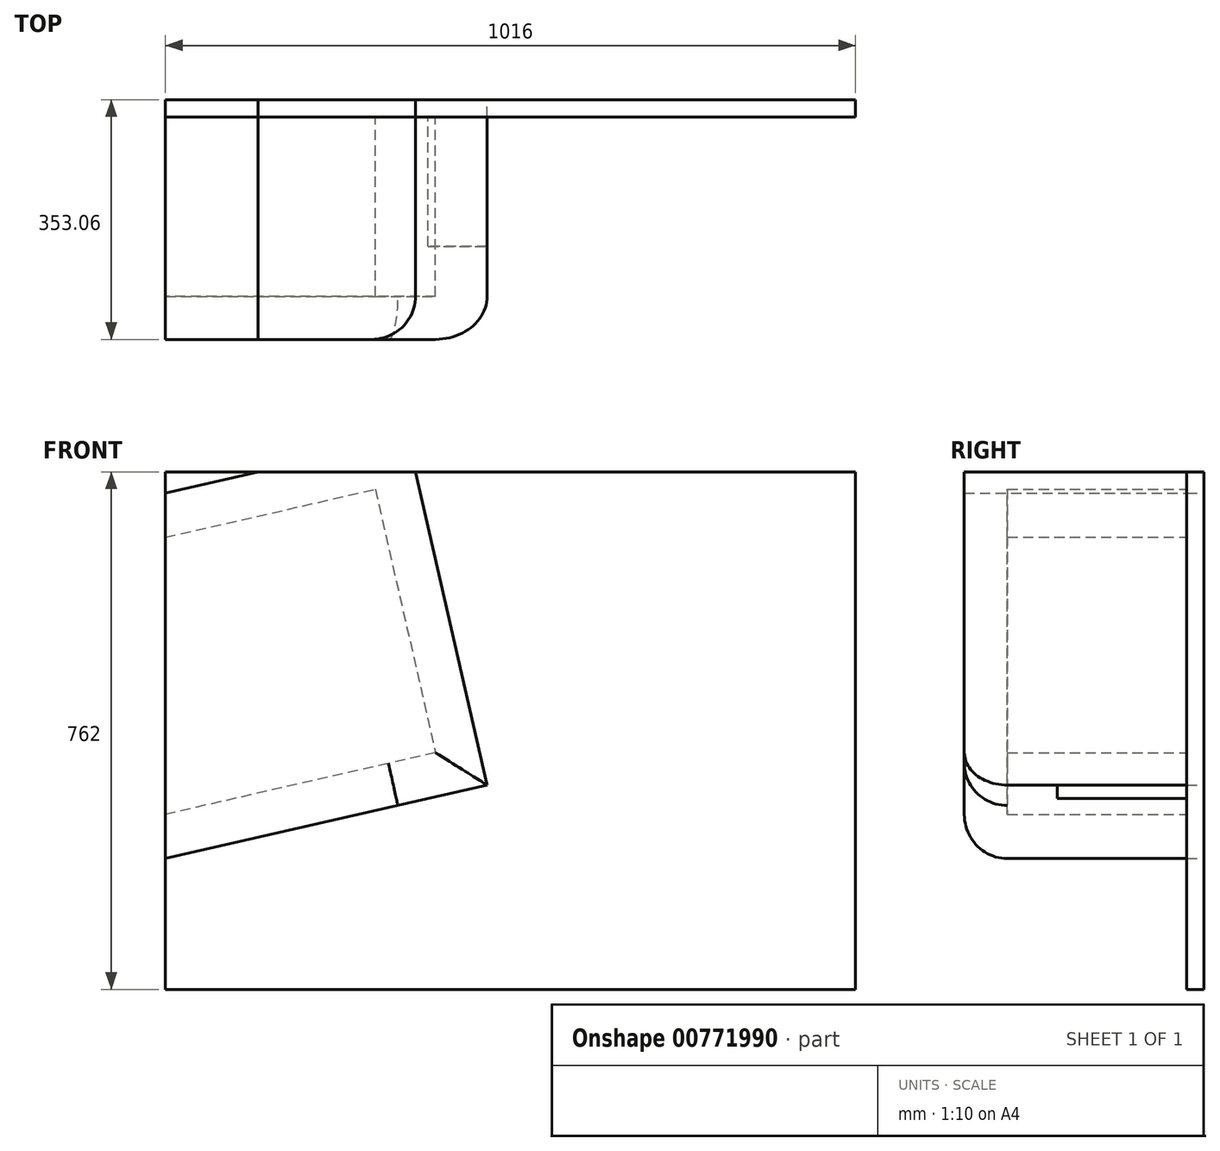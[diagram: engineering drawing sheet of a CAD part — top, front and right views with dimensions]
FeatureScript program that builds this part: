
annotation { "Feature Type Name" : "Feature", "Feature Type Description" : "" }
export const myFeature = defineFeature(function(context is Context, id is Id, definition is map)
    precondition{}
    {
        {
            var Q0;
            Q0=qCreatedBy(makeId("Front.planeOp"),FACE);
            var sketch = newSketch(context, id + "F0", { "sketchPlane" : qUnion([Q0])});
            skLineSegment(sketch, "E0.bottom", {"start": v(-68.95, 0) * mm, "end": v(-1084.95, 0) * mm});
            skLineSegment(sketch, "E0.top", {"start": v(-68.95, 762) * mm, "end": v(-1084.95, 762) * mm});
            skLineSegment(sketch, "E0.left", {"start": v(-68.95, 0) * mm, "end": v(-68.95, 762) * mm});
            skLineSegment(sketch, "E0.right", {"start": v(-1084.95, 0) * mm, "end": v(-1084.95, 762) * mm});
            skSolve(sketch);
        }
        {
            var Q0;
            Q0=makeQuery(id+"F0.imprint","IMPRINT",FACE,{"disambiguationData":[TD([[makeQuery(id+"F0.imprint","IMPRINT",EDGE,{"derivedFrom":sQuery(id+"F0.wireOp",EDGE,"E0.bottom")}),-1.0]])]});
            extrude(context, id + "F1", {"entities" : qUnion([Q0]), "depth" : 25.4 * mm, "offsetDistance" : 25.4 * mm});
        }
        {
            var Q0;
            Q0=makeQuery(id+"F1.opExtrude","CAP_FACE",FACE,{"disambiguationData":[OSD([sQuery(id+"F0.wireOp",EDGE,"E0.bottom"),sQuery(id+"F0.wireOp",EDGE,"E0.top"),sQuery(id+"F0.wireOp",EDGE,"E0.left"),sQuery(id+"F0.wireOp",EDGE,"E0.right")])],"isStart":false});
            var sketch = newSketch(context, id + "F2", { "sketchPlane" : qUnion([Q0])});
            skLineSegment(sketch, "E1", {"start": v(-1084.95, 665.71) * mm, "end": v(-845.45, 720.43) * mm});
            skLineSegment(sketch, "E2", {"start": v(-845.45, 720.43) * mm, "end": v(-756.87, 332.69) * mm});
            skLineSegment(sketch, "E3", {"start": v(-756.87, 332.69) * mm, "end": v(-1084.95, 257.73) * mm});
            skLineSegment(sketch, "E4", {"start": v(-1084.95, 665.71) * mm, "end": v(-776.09, 736.28) * mm});
            skLineSegment(sketch, "E5", {"start": v(-776.09, 736.28) * mm, "end": v(-687.5, 348.53) * mm});
            skLineSegment(sketch, "E6", {"start": v(-687.5, 348.53) * mm, "end": v(-756.87, 332.69) * mm});
            skSolve(sketch);
        }
        {
            var Q0;
            {var subQ0=sQuery(id+"F2.wireOp",EDGE,"E2");Q0=makeQuery(id+"F2.imprint","IMPRINT",FACE,{"disambiguationData":[TD([[makeQuery(id+"F2.imprint","IMPRINT",EDGE,{"derivedFrom":subQ0}),1.0]])]});}
            var Q1;
            {var subQ0=sQuery(id+"F2.wireOp",EDGE,"E2");Q1=makeQuery(id+"F2.imprint","IMPRINT",FACE,{"disambiguationData":[TD([[makeQuery(id+"F2.imprint","IMPRINT",EDGE,{"derivedFrom":subQ0}),-1.0]])]});}
            extrude(context, id + "F3", {"entities" : qUnion([Q0, Q1]), "depth" : 264.16 * mm, "offsetDistance" : 25.4 * mm});
        }
        {
            var Q0;
            Q0=makeQuery(id+"F3.opExtrude","SWEPT_FACE",FACE,{"disambiguationData":[OSD([sQuery(id+"F0.wireOp",EDGE,"E0.right")])]});
            shell(context, id + "F4", {"entities" : qUnion([Q0]), "thickness" : 63.5 * mm, "oppositeDirection" : true});
        }
        {
            var Q0;
            Q0=makeQuery(id+"F3.opExtrude","CAP_FACE",FACE,{"disambiguationData":[OSD([sQuery(id+"F0.wireOp",EDGE,"E0.right"),sQuery(id+"F2.wireOp",EDGE,"E3"),sQuery(id+"F2.wireOp",EDGE,"E4"),sQuery(id+"F2.wireOp",EDGE,"E5"),sQuery(id+"F2.wireOp",EDGE,"E6")])],"isStart":true});
            var Q1;
            {var subQ0=sQuery(id+"F2.wireOp",EDGE,"E6");var subQ1=sQuery(id+"F2.wireOp",EDGE,"E5");var subQ2=sQuery(id+"F2.wireOp",EDGE,"E4");var subQ3=sQuery(id+"F2.wireOp",EDGE,"E3");var subQ4=sQuery(id+"F0.wireOp",EDGE,"E0.right");Q1=makeQuery(id+"F4.opShell","OFFSET_FACE",FACE,{"disambiguationData":[OSD([subQ4,subQ3,subQ2,subQ1,subQ0]),TDD([makeQuery(id+"F3.opExtrude","CAP_FACE",FACE,{"disambiguationData":[OSD([subQ4,subQ3,subQ2,subQ1,subQ0])],"isStart":true})])]});}
            extrude(context, id + "F5", {"entities" : qUnion([Q0]), "operationType" : NewBodyOperationType.REMOVE, "endBound" : BoundingType.UP_TO_SURFACE, "oppositeDirection" : true, "depth" : 25.4 * mm, "endBoundEntityFace" : qUnion([Q1]), "offsetDistance" : 25.4 * mm});
        }
        {
            var Q0;
            Q0=makeQuery(id+"F5.boolean.opBoolean","COPY",FACE,{"derivedFrom":makeQuery(id+"F5.opExtrude","CAP_FACE",FACE,{"disambiguationData":[OSD([sQuery(id+"F0.wireOp",EDGE,"E0.right"),sQuery(id+"F2.wireOp",EDGE,"E3"),sQuery(id+"F2.wireOp",EDGE,"E4"),sQuery(id+"F2.wireOp",EDGE,"E5"),sQuery(id+"F2.wireOp",EDGE,"E6")])],"isStart":false})});
            var sketch = newSketch(context, id + "F6", { "sketchPlane" : qUnion([Q0])});
            skLineSegment(sketch, "E7", {"start": v(728.33, 812.32) * mm, "end": v(716.83, 762) * mm});
            skLineSegment(sketch, "E8", {"start": v(716.83, 762) * mm, "end": v(948.6, 762) * mm});
            skLineSegment(sketch, "E9", {"start": v(948.6, 762) * mm, "end": v(728.33, 812.32) * mm});
            skSolve(sketch);
        }
        {
            var Q0;
            Q0=makeQuery(id+"F6.imprint","IMPRINT",FACE,{"disambiguationData":[TD([[makeQuery(id+"F6.imprint","IMPRINT",EDGE,{"derivedFrom":sQuery(id+"F6.wireOp",EDGE,"E7")}),1.0]])]});
            extrude(context, id + "F7", {"entities" : qUnion([Q0]), "operationType" : NewBodyOperationType.REMOVE, "endBound" : BoundingType.THROUGH_ALL, "oppositeDirection" : true, "depth" : 25.4 * mm, "offsetDistance" : 25.4 * mm});
        }
        {
            var Q0;
            Q0=makeQuery(id+"F3.opExtrude","CAP_EDGE",EDGE,{"disambiguationData":[OSD([sQuery(id+"F2.wireOp",EDGE,"E3"),sQuery(id+"F2.wireOp",EDGE,"E6")])],"isStart":false});
            var Q1;
            Q1=makeQuery(id+"F3.opExtrude","CAP_EDGE",EDGE,{"disambiguationData":[OSD([sQuery(id+"F2.wireOp",EDGE,"E5")])],"isStart":false});
            fillet(context, id + "F8", {"entities" : qUnion([Q0, Q1]), "radius" : 63.5 * mm, "tangentPropagation" : true, "allowEdgeOverflow" : false});
        }
        {
            var Q0;
            Q0=makeQuery(id+"F1.opExtrude","CAP_FACE",FACE,{"disambiguationData":[OSD([sQuery(id+"F0.wireOp",EDGE,"E0.bottom"),sQuery(id+"F0.wireOp",EDGE,"E0.top"),sQuery(id+"F0.wireOp",EDGE,"E0.left"),sQuery(id+"F0.wireOp",EDGE,"E0.right")])],"isStart":false});
            var sketch = newSketch(context, id + "F9", { "sketchPlane" : qUnion([Q0])});
            skLineSegment(sketch, "E10", {"start": v(-698.43, 280.9) * mm, "end": v(-611.45, 300.77) * mm});
            skLineSegment(sketch, "E11", {"start": v(-611.45, 300.77) * mm, "end": v(-641.35, 431.65) * mm});
            skLineSegment(sketch, "E12", {"start": v(-641.35, 431.65) * mm, "end": v(-355.55, 235.03) * mm});
            skLineSegment(sketch, "E13", {"start": v(-355.55, 235.03) * mm, "end": v(-434.42, 130.1) * mm});
            skLineSegment(sketch, "E14", {"start": v(-434.42, 130.1) * mm, "end": v(-698.43, 280.9) * mm});
            skSolve(sketch);
        }
        {
            var Q0;
            Q0=makeQuery(id+"F9.imprint","IMPRINT",FACE,{"disambiguationData":[TD([[makeQuery(id+"F9.imprint","IMPRINT",EDGE,{"derivedFrom":sQuery(id+"F9.wireOp",EDGE,"E10")}),-1.0]])]});
            extrude(context, id + "F10", {"entities" : qUnion([Q0]), "depth" : 190.5 * mm, "offsetDistance" : 25.4 * mm});
        }
        {
            var Q0;
            Q0=makeQuery(id+"F10.opExtrude","SWEPT_FACE",FACE,{"disambiguationData":[OSD([sQuery(id+"F9.wireOp",EDGE,"E14")])]});
            var sketch = newSketch(context, id + "F11", { "sketchPlane" : qUnion([Q0])});
            skPoint(sketch, "E15.end.orphan", {"position": v(-441.75, 120.65) * mm});
            skLineSegment(sketch, "E16", {"start": v(-609.57, 215.9) * mm, "end": v(-407.55, 104.62) * mm});
            skLineSegment(sketch, "E17", {"start": v(-407.55, 104.62) * mm, "end": v(-407.55, 215.9) * mm});
            skLineSegment(sketch, "E18", {"start": v(-407.55, 215.9) * mm, "end": v(-609.57, 215.9) * mm});
            skSolve(sketch);
        }
        {
            var Q0;
            {var subQ0=sQuery(id+"F11.wireOp",EDGE,"E18");var subQ1=sQuery(id+"F11.wireOp",EDGE,"E16");var subQ2=sQuery(id+"F9.wireOp",EDGE,"E14");var subQ3=makeQuery(id+"F11.imprint","INTERSECT",VERTEX,{"derivedFrom":[makeQuery(id+"F10.opExtrude","CAP_EDGE",EDGE,{"disambiguationData":[OSD([subQ2])],"isStart":false}),subQ1,subQ0]});Q0=makeQuery(id+"F11.imprint","IMPRINT",FACE,{"disambiguationData":[TD([[makeQuery(id+"F11.imprint","IMPRINT",EDGE,{"disambiguationData":[TD([[subQ3,-1.0]])],"derivedFrom":subQ1}),1.0]])]});}
            var Q1;
            {var subQ0=sQuery(id+"F11.wireOp",EDGE,"E17");Q1=makeQuery(id+"F11.imprint","IMPRINT",FACE,{"disambiguationData":[TD([[makeQuery(id+"F11.imprint","IMPRINT",EDGE,{"derivedFrom":subQ0}),1.0]])]});}
            extrude(context, id + "F12", {"entities" : qUnion([Q0, Q1]), "operationType" : NewBodyOperationType.REMOVE, "endBound" : BoundingType.THROUGH_ALL, "oppositeDirection" : true, "depth" : 25.4 * mm, "offsetDistance" : 25.4 * mm});
        }
    });
